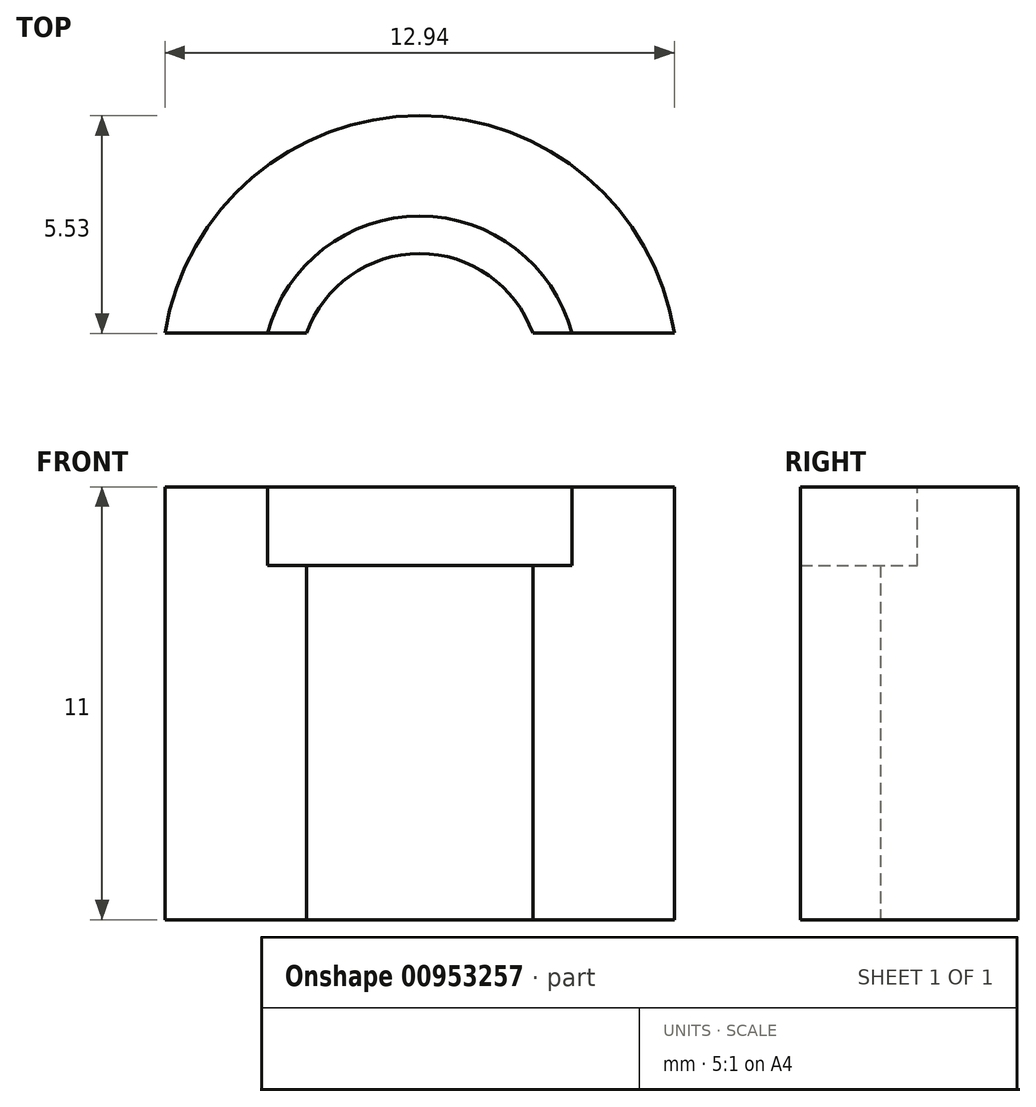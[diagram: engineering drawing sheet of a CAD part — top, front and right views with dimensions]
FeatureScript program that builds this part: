
annotation { "Feature Type Name" : "Feature", "Feature Type Description" : "" }
export const myFeature = defineFeature(function(context is Context, id is Id, definition is map)
    precondition{}
    {
        {
            var Q0;
            Q0=qCreatedBy(makeId("Top.planeOp"),FACE);
            var sketch = newSketch(context, id + "F0", { "sketchPlane" : qUnion([Q0])});
            skCircle(sketch, "E0", {"center": v(0, 0) * mm, "radius": 2.9 * mm, "construction": true});
            skArc(sketch, "E1.0", {"start": v(2.87, 1.03) * mm, "mid": v(0, 3.05) * mm, "end": v(-2.87, 1.03) * mm});
            skLineSegment(sketch, "E2.bottom", {"start": v(10, 0.88) * mm, "end": v(-10, 0.88) * mm, "construction": true});
            skLineSegment(sketch, "E2.top", {"start": v(10, -0.88) * mm, "end": v(-10, -0.88) * mm, "construction": true});
            skLineSegment(sketch, "E2.left", {"start": v(10, 0.88) * mm, "end": v(10, -0.87) * mm, "construction": true});
            skLineSegment(sketch, "E2.right", {"start": v(-10, 0.88) * mm, "end": v(-10, -0.87) * mm, "construction": true});
            skLineSegment(sketch, "E3.0", {"start": v(6.47, 1.03) * mm, "end": v(2.87, 1.03) * mm});
            skArc(sketch, "E4.0", {"start": v(6.47, 1.03) * mm, "mid": v(0, 6.55) * mm, "end": v(-6.47, 1.03) * mm});
            skLineSegment(sketch, "E5.trimOffspring", {"start": v(-2.87, 1.03) * mm, "end": v(-6.47, 1.03) * mm});
            skSolve(sketch);
        }
        {
            var Q0;
            Q0=makeQuery(id+"F0.imprint","IMPRINT",FACE,{"disambiguationData":[TD([[makeQuery(id+"F0.imprint","IMPRINT",EDGE,{"derivedFrom":sQuery(id+"F0.wireOp",EDGE,"E1.0")}),-1.0]])]});
            extrude(context, id + "F1", {"entities" : qUnion([Q0]), "depth" : 11 * mm, "offsetDistance" : 25 * mm});
        }
        {
            var Q0;
            Q0=makeQuery(id+"F1.opExtrude","CAP_FACE",FACE,{"disambiguationData":[OSD([sQuery(id+"F0.wireOp",EDGE,"E1.0"),sQuery(id+"F0.wireOp",EDGE,"E3.0"),sQuery(id+"F0.wireOp",EDGE,"E4.0"),sQuery(id+"F0.wireOp",EDGE,"E5.trimOffspring")])],"isStart":false});
            var sketch = newSketch(context, id + "F2", { "sketchPlane" : qUnion([Q0])});
            skCircle(sketch, "E6", {"center": v(0, 0) * mm, "radius": 4 * mm});
            skSolve(sketch);
        }
        {
            var Q0;
            {var subQ5=makeQuery(id+"F1.opExtrude","CAP_EDGE",EDGE,{"disambiguationData":[OSD([sQuery(id+"F0.wireOp",EDGE,"E1.0")])],"isStart":false});Q0=makeQuery(id+"F2.imprint","IMPRINT",FACE,{"disambiguationData":[TD([[makeQuery(id+"F2.imprint","IMPRINT",EDGE,{"derivedFrom":subQ5}),-1.0]])]});}
            var Q1;
            Q1=makeQuery(id+"F1.opExtrude","CAP_FACE",FACE,{"disambiguationData":[OSD([sQuery(id+"F0.wireOp",EDGE,"E1.0"),sQuery(id+"F0.wireOp",EDGE,"E3.0"),sQuery(id+"F0.wireOp",EDGE,"E4.0"),sQuery(id+"F0.wireOp",EDGE,"E5.trimOffspring")])],"isStart":true});
            extrude(context, id + "F3", {"entities" : qUnion([Q0]), "operationType" : NewBodyOperationType.REMOVE, "endBound" : BoundingType.UP_TO_SURFACE, "oppositeDirection" : true, "depth" : 25 * mm, "endBoundEntityFace" : qUnion([Q1]), "hasOffset" : true, "offsetDistance" : 9 * mm});
        }
    });
